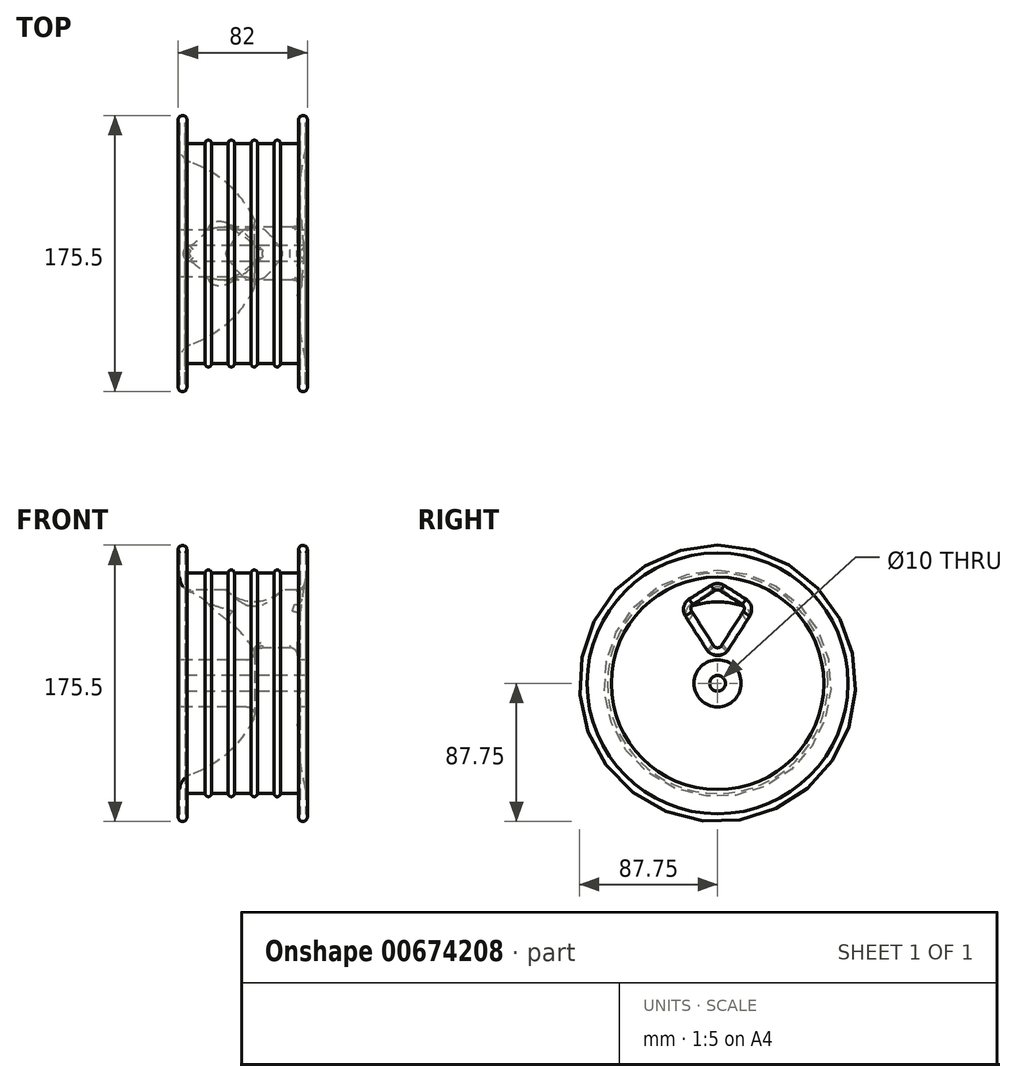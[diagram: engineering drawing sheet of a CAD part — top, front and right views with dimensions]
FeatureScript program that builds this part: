
annotation { "Feature Type Name" : "Feature", "Feature Type Description" : "" }
export const myFeature = defineFeature(function(context is Context, id is Id, definition is map)
    precondition{}
    {
        {
            var Q0;
            Q0=qCreatedBy(makeId("Front.planeOp"),FACE);
            var sketch = newSketch(context, id + "F0", { "sketchPlane" : qUnion([Q0])});
            skLineSegment(sketch, "E0", {"start": v(0, 85) * mm, "end": v(-3.5, 85) * mm});
            skLineSegment(sketch, "E1", {"start": v(-3.5, 85) * mm, "end": v(-3.5, 70) * mm});
            skLineSegment(sketch, "E2", {"start": v(-76.5, 70) * mm, "end": v(-76.5, 85) * mm});
            skLineSegment(sketch, "E3", {"start": v(-80, 85) * mm, "end": v(-80, 70) * mm});
            skLineSegment(sketch, "E4", {"start": v(-80, 0) * mm, "end": v(0, 0) * mm});
            skArc(sketch, "E5", {"start": v(0, 82.88) * mm, "mid": v(-1.75, 87.75) * mm, "end": v(-3.5, 82.88) * mm});
            skArc(sketch, "E6", {"start": v(-76.5, 82.88) * mm, "mid": v(-78.25, 87.75) * mm, "end": v(-80, 82.88) * mm});
            skLineSegment(sketch, "E7", {"start": v(-76.5, 70) * mm, "end": v(-61.9, 70) * mm});
            skLineSegment(sketch, "E8", {"start": v(-61.9, 70) * mm, "end": v(-47.3, 70) * mm});
            skLineSegment(sketch, "E9", {"start": v(-47.3, 70) * mm, "end": v(-32.7, 70) * mm});
            skLineSegment(sketch, "E10", {"start": v(-32.7, 70) * mm, "end": v(-18.1, 70) * mm});
            skLineSegment(sketch, "E11", {"start": v(-18.1, 70) * mm, "end": v(-3.5, 70) * mm});
            skArc(sketch, "E12", {"start": v(-16.1, 70) * mm, "mid": v(-18.1, 72) * mm, "end": v(-20.1, 70) * mm});
            skArc(sketch, "E13", {"start": v(-30.7, 70) * mm, "mid": v(-32.7, 72) * mm, "end": v(-34.7, 70) * mm});
            skArc(sketch, "E14", {"start": v(-45.3, 70) * mm, "mid": v(-47.3, 72) * mm, "end": v(-49.3, 70) * mm});
            skArc(sketch, "E15", {"start": v(-59.9, 70) * mm, "mid": v(-61.9, 72) * mm, "end": v(-63.9, 70) * mm});
            skLineSegment(sketch, "E16", {"start": v(-80, 70) * mm, "end": v(-80, 67.5) * mm});
            skLineSegment(sketch, "E17", {"start": v(-80, 0) * mm, "end": v(-80, 15) * mm});
            skLineSegment(sketch, "E18", {"start": v(-80, 15) * mm, "end": v(-37.47, 15) * mm});
            skArc(sketch, "E19", {"start": v(-32.96, 22.16) * mm, "mid": v(-49.51, 44.14) * mm, "end": v(-73.26, 58.05) * mm});
            skPoint(sketch, "E20.visualSharp", {"position": v(-80, 60) * mm});
            skArc(sketch, "E20.filletArc", {"start": v(-80, 67.5) * mm, "mid": v(-78.14, 61.7) * mm, "end": v(-73.26, 58.05) * mm});
            skPoint(sketch, "E21.visualSharp", {"position": v(-30, 15) * mm});
            skArc(sketch, "E22.filletArc", {"start": v(-37.47, 15) * mm, "mid": v(-33.24, 17.34) * mm, "end": v(-32.96, 22.16) * mm});
            skLineSegment(sketch, "E23", {"start": v(0, 0) * mm, "end": v(0, 15) * mm});
            skPoint(sketch, "E23.endSnap0", {"position": v(-58.74, 15) * mm});
            skLineSegment(sketch, "E24", {"start": v(-5, 15) * mm, "end": v(0, 15) * mm});
            skArc(sketch, "E25", {"start": v(0, 67.5) * mm, "mid": v(-4.24, 41.42) * mm, "end": v(-5, 15) * mm});
            skLineSegment(sketch, "E26", {"start": v(0, 85) * mm, "end": v(0, 67.5) * mm});
            skSolve(sketch);
        }
        {
            var Q0;
            {var subQ15=sQuery(id+"F0.wireOp",EDGE,"E4");Q0=makeQuery(id+"F0.imprint","IMPRINT",FACE,{"disambiguationData":[TD([[makeQuery(id+"F0.imprint","IMPRINT",EDGE,{"derivedFrom":subQ15}),1.0]])]});}
            var Q1;
            {var subQ0=sQuery(id+"F0.wireOp",EDGE,"E10");var subQ1=sQuery(id+"F0.wireOp",EDGE,"E9");var subQ2=makeQuery(id+"F0.imprint","INTERSECT",VERTEX,{"derivedFrom":[subQ1,subQ0]});Q1=makeQuery(id+"F0.imprint","IMPRINT",FACE,{"disambiguationData":[TD([[makeQuery(id+"F0.imprint","IMPRINT",EDGE,{"disambiguationData":[TD([[subQ2,1.0]])],"derivedFrom":subQ1}),1.0]])]});}
            var Q2;
            {var subQ0=sQuery(id+"F0.wireOp",EDGE,"E9");var subQ1=sQuery(id+"F0.wireOp",EDGE,"E8");var subQ2=makeQuery(id+"F0.imprint","INTERSECT",VERTEX,{"derivedFrom":[subQ1,subQ0]});Q2=makeQuery(id+"F0.imprint","IMPRINT",FACE,{"disambiguationData":[TD([[makeQuery(id+"F0.imprint","IMPRINT",EDGE,{"disambiguationData":[TD([[subQ2,1.0]])],"derivedFrom":subQ1}),1.0]])]});}
            var Q3;
            {var subQ0=sQuery(id+"F0.wireOp",EDGE,"E8");var subQ1=sQuery(id+"F0.wireOp",EDGE,"E7");var subQ2=makeQuery(id+"F0.imprint","INTERSECT",VERTEX,{"derivedFrom":[subQ1,subQ0]});Q3=makeQuery(id+"F0.imprint","IMPRINT",FACE,{"disambiguationData":[TD([[makeQuery(id+"F0.imprint","IMPRINT",EDGE,{"disambiguationData":[TD([[subQ2,1.0]])],"derivedFrom":subQ1}),1.0]])]});}
            var Q4;
            {var subQ0=sQuery(id+"F0.wireOp",EDGE,"zVJpPXV0-3Wk5-ReZu-829z-St5m1WfWDI6h");Q4=makeQuery(id+"F0.imprint","IMPRINT",FACE,{"disambiguationData":[TD([[makeQuery(id+"F0.imprint","IMPRINT",EDGE,{"derivedFrom":subQ0}),-1.0]])]});}
            var Q5;
            {var subQ0=sQuery(id+"F0.wireOp",EDGE,"E0");Q5=makeQuery(id+"F0.imprint","IMPRINT",FACE,{"disambiguationData":[TD([[makeQuery(id+"F0.imprint","IMPRINT",EDGE,{"derivedFrom":subQ0}),-1.0]])]});}
            var Q6;
            {var subQ0=sQuery(id+"F0.wireOp",EDGE,"E11");var subQ1=sQuery(id+"F0.wireOp",EDGE,"E10");var subQ2=makeQuery(id+"F0.imprint","INTERSECT",VERTEX,{"derivedFrom":[subQ1,subQ0]});Q6=makeQuery(id+"F0.imprint","IMPRINT",FACE,{"disambiguationData":[TD([[makeQuery(id+"F0.imprint","IMPRINT",EDGE,{"disambiguationData":[TD([[subQ2,1.0]])],"derivedFrom":subQ1}),1.0]])]});}
            var Q7;
            Q7=sQuery(id+"F0.wireOp",EDGE,"E4");
            revolve(context, id + "F1", {"entities" : qUnion([Q0, Q1, Q2, Q3, Q4, Q5, Q6]), "axis" : qUnion([Q7]), "revolveType" : RevolveType.FULL});
        }
        {
            var Q0;
            Q0=makeQuery(id+"F1.opRevolve","SWEPT_FACE",FACE,{"disambiguationData":[OSD([sQuery(id+"F0.wireOp",EDGE,"E17")])]});
            var sketch = newSketch(context, id + "F2", { "sketchPlane" : qUnion([Q0])});
            skCircle(sketch, "E27", {"center": v(0, 0) * mm, "radius": 5 * mm});
            skSolve(sketch);
        }
        {
            var Q0;
            Q0 = qSketchRegion(id + "F2", true);
            var Q1;
            Q1=makeQuery(id+"F1.opRevolve","SWEPT_FACE",FACE,{"disambiguationData":[OSD([sQuery(id+"F0.wireOp",EDGE,"E23")])]});
            extrude(context, id + "F3", {"entities" : qUnion([Q0]), "operationType" : NewBodyOperationType.REMOVE, "endBound" : BoundingType.UP_TO_SURFACE, "oppositeDirection" : true, "depth" : 25 * mm, "endBoundEntityFace" : qUnion([Q1]), "offsetDistance" : 25 * mm});
        }
        {
            var Q0;
            Q0=makeQuery(id+"F1.opRevolve","SWEPT_FACE",FACE,{"disambiguationData":[OSD([sQuery(id+"F0.wireOp",EDGE,"E3"),sQuery(id+"F0.wireOp",EDGE,"E16")])]});
            var sketch = newSketch(context, id + "F4", { "sketchPlane" : qUnion([Q0])});
            skLineSegment(sketch, "E28", {"start": v(2.53, 23.97) * mm, "end": v(16.51, 45.92) * mm});
            skLineSegment(sketch, "E29", {"start": v(15.6, 50.06) * mm, "end": v(1.61, 58.97) * mm});
            skLineSegment(sketch, "E30", {"start": v(-1.61, 58.97) * mm, "end": v(-15.6, 50.06) * mm});
            skLineSegment(sketch, "E31", {"start": v(-16.51, 45.92) * mm, "end": v(-2.53, 23.97) * mm});
            skPoint(sketch, "E32.visualSharp", {"position": v(-18.13, 48.45) * mm});
            skArc(sketch, "E32.filletArc", {"start": v(-15.6, 50.06) * mm, "mid": v(-16.91, 48.18) * mm, "end": v(-16.51, 45.92) * mm});
            skPoint(sketch, "E33.visualSharp", {"position": v(0, 60) * mm});
            skArc(sketch, "E33.filletArc", {"start": v(1.61, 58.97) * mm, "mid": v(0, 59.44) * mm, "end": v(-1.61, 58.97) * mm});
            skPoint(sketch, "E34.visualSharp", {"position": v(18.13, 48.45) * mm});
            skArc(sketch, "E34.filletArc", {"start": v(16.51, 45.92) * mm, "mid": v(16.91, 48.18) * mm, "end": v(15.6, 50.06) * mm});
            skPoint(sketch, "E35.visualSharp", {"position": v(0, 20) * mm});
            skArc(sketch, "E35.filletArc", {"start": v(-2.53, 23.97) * mm, "mid": v(-1.28, 22.87) * mm, "end": v(0.35, 22.6) * mm});
            skPoint(sketch, "E36.visualSharp", {"position": v(2.53, 23.97) * mm});
            skArc(sketch, "E36.filletArc", {"start": v(0.35, 22.6) * mm, "mid": v(1.6, 23.04) * mm, "end": v(2.53, 23.97) * mm});
            skSolve(sketch);
        }
        {
            var Q0;
            Q0 = qSketchRegion(id + "F4", true);
            var Q1;
            Q1=makeQuery(id+"F1.opRevolve","SWEPT_FACE",FACE,{"disambiguationData":[OSD([sQuery(id+"F0.wireOp",EDGE,"E23")])]});
            extrude(context, id + "F5", {"entities" : qUnion([Q0]), "operationType" : NewBodyOperationType.REMOVE, "endBound" : BoundingType.UP_TO_SURFACE, "oppositeDirection" : true, "depth" : 25 * mm, "endBoundEntityFace" : qUnion([Q1]), "offsetDistance" : 25 * mm});
        }
        {
            var Q0;
            Q0=makeQuery(id+"F5.boolean.opBoolean","INTERSECT",EDGE,{"derivedFrom":[makeQuery(id+"F1.opRevolve","SWEPT_FACE",FACE,{"disambiguationData":[OSD([sQuery(id+"F0.wireOp",EDGE,"E19")])]}),makeQuery(id+"F5.opExtrude","SWEPT_FACE",FACE,{"disambiguationData":[OSD([sQuery(id+"F4.wireOp",EDGE,"E28")])]})]});
            var Q1;
            Q1=makeQuery(id+"F5.boolean.opBoolean","INTERSECT",EDGE,{"derivedFrom":[makeQuery(id+"F1.opRevolve","SWEPT_FACE",FACE,{"disambiguationData":[OSD([sQuery(id+"F0.wireOp",EDGE,"E19")])]}),makeQuery(id+"F5.opExtrude","SWEPT_FACE",FACE,{"disambiguationData":[OSD([sQuery(id+"F4.wireOp",EDGE,"E29")])]})]});
            var Q2;
            Q2=makeQuery(id+"F5.boolean.opBoolean","INTERSECT",EDGE,{"derivedFrom":[makeQuery(id+"F1.opRevolve","SWEPT_FACE",FACE,{"disambiguationData":[OSD([sQuery(id+"F0.wireOp",EDGE,"E19")])]}),makeQuery(id+"F5.opExtrude","SWEPT_FACE",FACE,{"disambiguationData":[OSD([sQuery(id+"F4.wireOp",EDGE,"E34.filletArc")])]})]});
            var Q3;
            Q3=makeQuery(id+"F5.boolean.opBoolean","INTERSECT",EDGE,{"derivedFrom":[makeQuery(id+"F1.opRevolve","SWEPT_FACE",FACE,{"disambiguationData":[OSD([sQuery(id+"F0.wireOp",EDGE,"E19")])]}),makeQuery(id+"F5.opExtrude","SWEPT_FACE",FACE,{"disambiguationData":[OSD([sQuery(id+"F4.wireOp",EDGE,"E35.filletArc"),sQuery(id+"F4.wireOp",EDGE,"E36.filletArc")])]})]});
            var Q4;
            Q4=makeQuery(id+"F5.boolean.opBoolean","INTERSECT",EDGE,{"derivedFrom":[makeQuery(id+"F1.opRevolve","SWEPT_FACE",FACE,{"disambiguationData":[OSD([sQuery(id+"F0.wireOp",EDGE,"E19")])]}),makeQuery(id+"F5.opExtrude","SWEPT_FACE",FACE,{"disambiguationData":[OSD([sQuery(id+"F4.wireOp",EDGE,"E31")])]})]});
            var Q5;
            Q5=makeQuery(id+"F5.boolean.opBoolean","INTERSECT",EDGE,{"derivedFrom":[makeQuery(id+"F1.opRevolve","SWEPT_FACE",FACE,{"disambiguationData":[OSD([sQuery(id+"F0.wireOp",EDGE,"E19")])]}),makeQuery(id+"F5.opExtrude","SWEPT_FACE",FACE,{"disambiguationData":[OSD([sQuery(id+"F4.wireOp",EDGE,"E32.filletArc")])]})]});
            var Q6;
            Q6=makeQuery(id+"F5.boolean.opBoolean","INTERSECT",EDGE,{"derivedFrom":[makeQuery(id+"F1.opRevolve","SWEPT_FACE",FACE,{"disambiguationData":[OSD([sQuery(id+"F0.wireOp",EDGE,"E19")])]}),makeQuery(id+"F5.opExtrude","SWEPT_FACE",FACE,{"disambiguationData":[OSD([sQuery(id+"F4.wireOp",EDGE,"E30")])]})]});
            var Q7;
            Q7=makeQuery(id+"F5.boolean.opBoolean","INTERSECT",EDGE,{"derivedFrom":[makeQuery(id+"F1.opRevolve","SWEPT_FACE",FACE,{"disambiguationData":[OSD([sQuery(id+"F0.wireOp",EDGE,"E20.filletArc")])]}),makeQuery(id+"F5.opExtrude","SWEPT_FACE",FACE,{"disambiguationData":[OSD([sQuery(id+"F4.wireOp",EDGE,"E33.filletArc")])]})]});
            var Q8;
            Q8=makeQuery(id+"F5.boolean.opBoolean","INTERSECT",EDGE,{"derivedFrom":[makeQuery(id+"F1.opRevolve","SWEPT_FACE",FACE,{"disambiguationData":[OSD([sQuery(id+"F0.wireOp",EDGE,"E20.filletArc")])]}),makeQuery(id+"F5.opExtrude","SWEPT_FACE",FACE,{"disambiguationData":[OSD([sQuery(id+"F4.wireOp",EDGE,"E29")])]})]});
            var Q9;
            Q9=makeQuery(id+"F5.boolean.opBoolean","INTERSECT",EDGE,{"derivedFrom":[makeQuery(id+"F1.opRevolve","SWEPT_FACE",FACE,{"disambiguationData":[OSD([sQuery(id+"F0.wireOp",EDGE,"E20.filletArc")])]}),makeQuery(id+"F5.opExtrude","SWEPT_FACE",FACE,{"disambiguationData":[OSD([sQuery(id+"F4.wireOp",EDGE,"E30")])]})]});
            var Q10;
            Q10=makeQuery(id+"F5.boolean.opBoolean","INTERSECT",EDGE,{"derivedFrom":[makeQuery(id+"F1.opRevolve","SWEPT_FACE",FACE,{"disambiguationData":[OSD([sQuery(id+"F0.wireOp",EDGE,"E25")])]}),makeQuery(id+"F5.opExtrude","SWEPT_FACE",FACE,{"disambiguationData":[OSD([sQuery(id+"F4.wireOp",EDGE,"E29")])]})]});
            var Q11;
            Q11=makeQuery(id+"F5.boolean.opBoolean","INTERSECT",EDGE,{"derivedFrom":[makeQuery(id+"F1.opRevolve","SWEPT_FACE",FACE,{"disambiguationData":[OSD([sQuery(id+"F0.wireOp",EDGE,"E25")])]}),makeQuery(id+"F5.opExtrude","SWEPT_FACE",FACE,{"disambiguationData":[OSD([sQuery(id+"F4.wireOp",EDGE,"E33.filletArc")])]})]});
            fillet(context, id + "F6", {"entities" : qUnion([Q0, Q1, Q2, Q3, Q4, Q5, Q6, Q7, Q8, Q9, Q10, Q11]), "radius" : 5 * mm, "tangentPropagation" : true, "allowEdgeOverflow" : false});
        }
        {
            var Q0;
            Q0=qCreatedBy(makeId("Front.planeOp"),FACE);
            var sketch = newSketch(context, id + "F7", { "sketchPlane" : qUnion([Q0])});
            skArc(sketch, "E37.0", {"start": v(-80, 67.5) * mm, "mid": v(-78.14, 61.7) * mm, "end": v(-73.26, 58.05) * mm});
            skArc(sketch, "E38.0", {"start": v(-32.96, 22.16) * mm, "mid": v(-49.51, 44.14) * mm, "end": v(-73.26, 58.05) * mm});
            skArc(sketch, "E39.0", {"start": v(-37.47, 15) * mm, "mid": v(-33.24, 17.34) * mm, "end": v(-32.96, 22.16) * mm});
            skLineSegment(sketch, "E40.0", {"start": v(-80, 15) * mm, "end": v(-37.47, 15) * mm});
            skLineSegment(sketch, "E41.0", {"start": v(-76.5, 70) * mm, "end": v(-61.9, 70) * mm});
            skPoint(sketch, "E42.0", {"position": v(-54.6, 70) * mm});
            skLineSegment(sketch, "E43.0", {"start": v(-61.9, 70) * mm, "end": v(-47.3, 70) * mm});
            skLineSegment(sketch, "E44.0", {"start": v(-47.3, 70) * mm, "end": v(-32.7, 70) * mm});
            skLineSegment(sketch, "E45.0", {"start": v(-32.7, 70) * mm, "end": v(-18.1, 70) * mm});
            skLineSegment(sketch, "E46", {"start": v(-76.5, 70) * mm, "end": v(-61.9, 65.58) * mm});
            skArc(sketch, "E47", {"start": v(-49.92, 58.62) * mm, "mid": v(-55.5, 62.8) * mm, "end": v(-61.9, 65.58) * mm});
            skArc(sketch, "E48", {"start": v(-49.92, 58.62) * mm, "mid": v(-32.7, 51.74) * mm, "end": v(-15.48, 58.62) * mm});
            skLineSegment(sketch, "E49.0", {"start": v(-18.1, 70) * mm, "end": v(-3.5, 70) * mm});
            skLineSegment(sketch, "E50", {"start": v(-3.5, 70) * mm, "end": v(-15.48, 58.62) * mm});
            skSolve(sketch);
        }
        {
            var Q0;
            Q0=makeQuery(id+"F7.imprint","IMPRINT",FACE,{"disambiguationData":[TD([[makeQuery(id+"F7.imprint","IMPRINT",EDGE,{"derivedFrom":sQuery(id+"F7.wireOp",EDGE,"E41.0")}),-1.0]])]});
            var Q1;
            Q1=sQuery(id+"F0.wireOp",EDGE,"E4");
            revolve(context, id + "F8", {"operationType" : NewBodyOperationType.ADD, "entities" : qUnion([Q0]), "axis" : qUnion([Q1]), "revolveType" : RevolveType.FULL});
        }
    });
